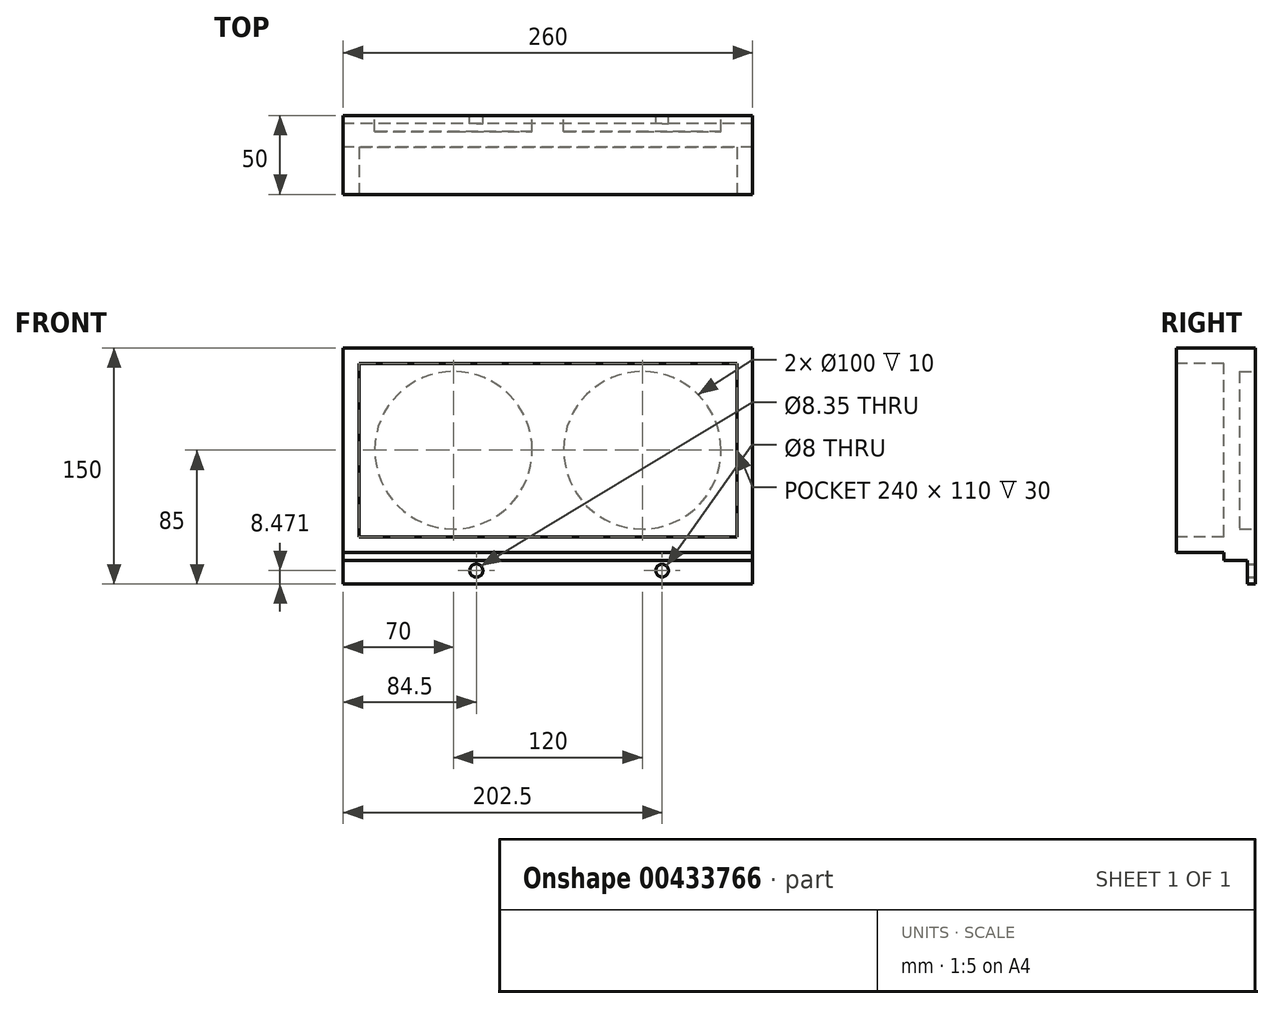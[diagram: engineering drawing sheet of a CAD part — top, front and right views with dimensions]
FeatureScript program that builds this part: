
annotation { "Feature Type Name" : "Feature", "Feature Type Description" : "" }
export const myFeature = defineFeature(function(context is Context, id is Id, definition is map)
    precondition{}
    {
        {
            var Q0;
            Q0=qCreatedBy(makeId("Front.planeOp"),FACE);
            var sketch = newSketch(context, id + "F0", { "sketchPlane" : qUnion([Q0])});
            skLineSegment(sketch, "E0.bottom", {"start": v(130, -65) * mm, "end": v(-130, -65) * mm});
            skLineSegment(sketch, "E0.top", {"start": v(130, 65) * mm, "end": v(-130, 65) * mm});
            skLineSegment(sketch, "E0.left", {"start": v(130, -65) * mm, "end": v(130, 65) * mm});
            skLineSegment(sketch, "E0.right", {"start": v(-130, -65) * mm, "end": v(-130, 65) * mm});
            skPoint(sketch, "E0.middle", {"position": v(0, 0) * mm});
            skSolve(sketch);
        }
        {
            var Q0;
            Q0=makeQuery(id+"F0.imprint","IMPRINT",FACE,{"disambiguationData":[TD([[makeQuery(id+"F0.imprint","IMPRINT",EDGE,{"derivedFrom":sQuery(id+"F0.wireOp",EDGE,"E0.bottom")}),-1.0]])]});
            extrude(context, id + "F1", {"entities" : qUnion([Q0]), "depth" : 50 * mm});
        }
        {
            var Q0;
            Q0=makeQuery(id+"F1.opExtrude","CAP_FACE",FACE,{"disambiguationData":[OSD([sQuery(id+"F0.wireOp",EDGE,"E0.bottom"),sQuery(id+"F0.wireOp",EDGE,"E0.top"),sQuery(id+"F0.wireOp",EDGE,"E0.left"),sQuery(id+"F0.wireOp",EDGE,"E0.right")])],"isStart":true});
            var sketch = newSketch(context, id + "F2", { "sketchPlane" : qUnion([Q0])});
            skCircle(sketch, "E1", {"center": v(60, 0) * mm, "radius": 50 * mm});
            skCircle(sketch, "E2", {"center": v(-60, 0) * mm, "radius": 50 * mm});
            skSolve(sketch);
        }
        {
            var Q0;
            Q0=makeQuery(id+"F2.imprint","IMPRINT",FACE,{"disambiguationData":[TD([[makeQuery(id+"F2.imprint","IMPRINT",EDGE,{"derivedFrom":sQuery(id+"F2.wireOp",EDGE,"E1")}),1.0]])]});
            var Q1;
            Q1=makeQuery(id+"F2.imprint","IMPRINT",FACE,{"disambiguationData":[TD([[makeQuery(id+"F2.imprint","IMPRINT",EDGE,{"derivedFrom":sQuery(id+"F2.wireOp",EDGE,"E2")}),1.0]])]});
            extrude(context, id + "F3", {"entities" : qUnion([Q0, Q1]), "operationType" : NewBodyOperationType.REMOVE, "oppositeDirection" : true, "depth" : 10 * mm});
        }
        {
            var Q0;
            Q0=makeQuery(id+"F1.opExtrude","CAP_FACE",FACE,{"disambiguationData":[OSD([sQuery(id+"F0.wireOp",EDGE,"E0.bottom"),sQuery(id+"F0.wireOp",EDGE,"E0.top"),sQuery(id+"F0.wireOp",EDGE,"E0.left"),sQuery(id+"F0.wireOp",EDGE,"E0.right")])],"isStart":false});
            var sketch = newSketch(context, id + "F4", { "sketchPlane" : qUnion([Q0])});
            skLineSegment(sketch, "E3.bottom", {"start": v(-120, -55) * mm, "end": v(120, -55) * mm});
            skLineSegment(sketch, "E3.top", {"start": v(-120, 55) * mm, "end": v(120, 55) * mm});
            skLineSegment(sketch, "E3.left", {"start": v(-120, -55) * mm, "end": v(-120, 55) * mm});
            skLineSegment(sketch, "E3.right", {"start": v(120, -55) * mm, "end": v(120, 55) * mm});
            skPoint(sketch, "E3.middle", {"position": v(0, 0) * mm});
            skSolve(sketch);
        }
        {
            var Q0;
            Q0=makeQuery(id+"F4.imprint","IMPRINT",FACE,{"disambiguationData":[TD([[makeQuery(id+"F4.imprint","IMPRINT",EDGE,{"derivedFrom":sQuery(id+"F4.wireOp",EDGE,"E3.bottom")}),1.0]])]});
            extrude(context, id + "F5", {"entities" : qUnion([Q0]), "operationType" : NewBodyOperationType.REMOVE, "oppositeDirection" : true, "depth" : 30 * mm});
        }
        {
            var Q0;
            Q0=makeQuery(id+"F1.opExtrude","SWEPT_FACE",FACE,{"disambiguationData":[OSD([sQuery(id+"F0.wireOp",EDGE,"E0.right")])]});
            var sketch = newSketch(context, id + "F6", { "sketchPlane" : qUnion([Q0])});
            skLineSegment(sketch, "E4", {"start": v(0, -65) * mm, "end": v(0, -85) * mm});
            skLineSegment(sketch, "E5", {"start": v(0, -85) * mm, "end": v(5, -85) * mm});
            skLineSegment(sketch, "E6", {"start": v(5, -85) * mm, "end": v(5, -70) * mm});
            skLineSegment(sketch, "E7", {"start": v(5, -70) * mm, "end": v(20, -70) * mm});
            skLineSegment(sketch, "E8", {"start": v(20, -70) * mm, "end": v(20, -65) * mm});
            skLineSegment(sketch, "E9", {"start": v(20, -65) * mm, "end": v(0, -65) * mm});
            skSolve(sketch);
        }
        {
            var Q0;
            Q0=makeQuery(id+"F6.imprint","IMPRINT",FACE,{"disambiguationData":[TD([[makeQuery(id+"F6.imprint","IMPRINT",EDGE,{"derivedFrom":sQuery(id+"F6.wireOp",EDGE,"E4")}),1.0]])]});
            extrude(context, id + "F7", {"entities" : qUnion([Q0]), "operationType" : NewBodyOperationType.ADD, "oppositeDirection" : true, "depth" : 260 * mm});
        }
        {
            var Q0;
            Q0=makeQuery(id+"F7.boolean.opBoolean","MERGE",FACE,{"derivedFrom":[makeQuery(id+"F1.opExtrude","CAP_FACE",FACE,{"disambiguationData":[OSD([sQuery(id+"F0.wireOp",EDGE,"E0.bottom"),sQuery(id+"F0.wireOp",EDGE,"E0.top"),sQuery(id+"F0.wireOp",EDGE,"E0.left"),sQuery(id+"F0.wireOp",EDGE,"E0.right")])],"isStart":true}),makeQuery(id+"F7.opExtrude","SWEPT_FACE",FACE,{"disambiguationData":[OSD([sQuery(id+"F6.wireOp",EDGE,"E4")])]})]});
            var sketch = newSketch(context, id + "F8", { "sketchPlane" : qUnion([Q0])});
            skCircle(sketch, "E10", {"center": v(45.5, -76.53) * mm, "radius": 4.18 * mm});
            skCircle(sketch, "E11", {"center": v(-72.5, -76.53) * mm, "radius": 4 * mm});
            skSolve(sketch);
        }
        {
            var Q0;
            Q0=makeQuery(id+"F8.imprint","IMPRINT",FACE,{"disambiguationData":[TD([[makeQuery(id+"F8.imprint","IMPRINT",EDGE,{"derivedFrom":sQuery(id+"F8.wireOp",EDGE,"E11")}),1.0]])]});
            var Q1;
            Q1=makeQuery(id+"F8.imprint","IMPRINT",FACE,{"disambiguationData":[TD([[makeQuery(id+"F8.imprint","IMPRINT",EDGE,{"derivedFrom":sQuery(id+"F8.wireOp",EDGE,"E10")}),1.0]])]});
            extrude(context, id + "F9", {"entities" : qUnion([Q0, Q1]), "operationType" : NewBodyOperationType.REMOVE, "oppositeDirection" : true, "depth" : 25 * mm});
        }
    });
